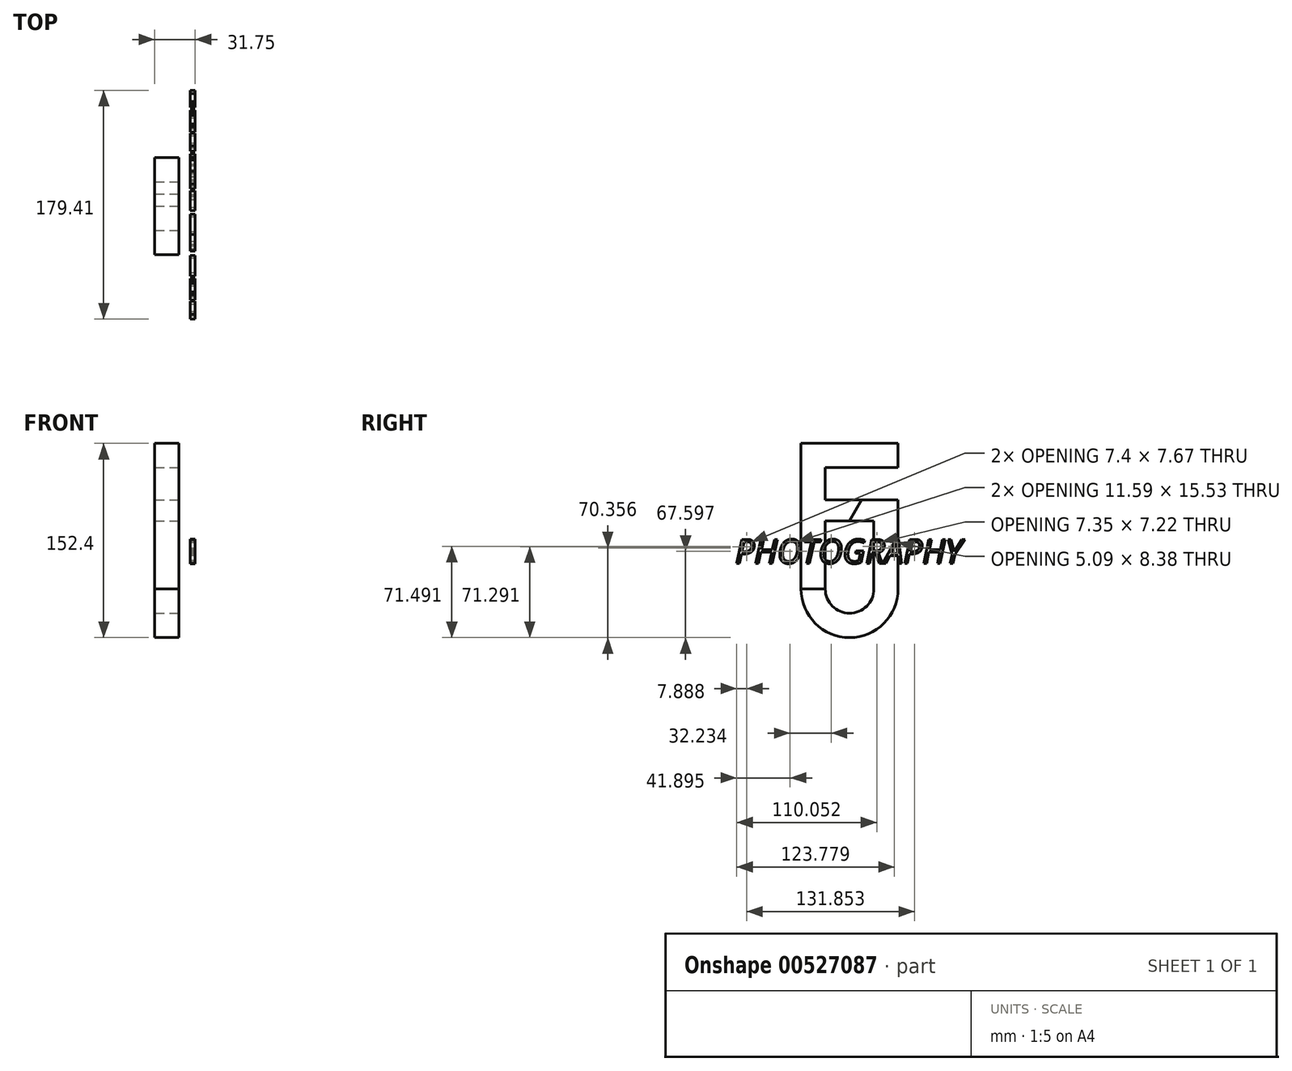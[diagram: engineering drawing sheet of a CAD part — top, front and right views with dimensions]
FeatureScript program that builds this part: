
annotation { "Feature Type Name" : "Feature", "Feature Type Description" : "" }
export const myFeature = defineFeature(function(context is Context, id is Id, definition is map)
    precondition{}
    {
        {
            var Q0;
            Q0=qCreatedBy(makeId("Right.planeOp"),FACE);
            var sketch = newSketch(context, id + "F0", { "sketchPlane" : qUnion([Q0])});
            skArc(sketch, "E0", {"start": v(-38.1, 0) * mm, "mid": v(0, -38.1) * mm, "end": v(38.1, 0) * mm});
            skArc(sketch, "E1", {"start": v(-19.05, 0) * mm, "mid": v(0, -19.05) * mm, "end": v(19.05, 0) * mm});
            skLineSegment(sketch, "E2", {"start": v(-38.1, 0) * mm, "end": v(-19.05, 0) * mm});
            skPoint(sketch, "E3.orphan", {"position": v(-52.53, 0) * mm});
            skLineSegment(sketch, "E4.top", {"start": v(-38.1, 114.3) * mm, "end": v(38.1, 114.3) * mm});
            skLineSegment(sketch, "E5", {"start": v(-19.05, 0) * mm, "end": v(-19.05, 53.35) * mm});
            skLineSegment(sketch, "E6", {"start": v(19.05, 0) * mm, "end": v(19.05, 53.35) * mm});
            skLineSegment(sketch, "E7", {"start": v(-19.05, 69.85) * mm, "end": v(9.52, 69.85) * mm});
            skPoint(sketch, "E8.start.orphan", {"position": v(24.72, 69.46) * mm});
            skPoint(sketch, "E9.trimOffspring.end.orphan", {"position": v(-24.72, 69.46) * mm});
            skLineSegment(sketch, "E10.trimOffspring", {"start": v(38.1, 95.25) * mm, "end": v(-19.05, 95.25) * mm});
            skLineSegment(sketch, "E11.trimOffspring", {"start": v(-19.05, 69.85) * mm, "end": v(-19.05, 95.25) * mm});
            skLineSegment(sketch, "E12", {"start": v(-38.1, 0) * mm, "end": v(-38.1, 114.3) * mm});
            skLineSegment(sketch, "E13", {"start": v(38.1, 0) * mm, "end": v(38.1, 69.85) * mm});
            skLineSegment(sketch, "E14.trimOffspring", {"start": v(38.1, 95.25) * mm, "end": v(38.1, 114.3) * mm});
            skLineSegment(sketch, "E15", {"start": v(-19.05, 53.35) * mm, "end": v(0, 53.35) * mm});
            skLineSegment(sketch, "E16", {"start": v(0, 53.35) * mm, "end": v(9.52, 69.85) * mm});
            skLineSegment(sketch, "E17", {"start": v(0, 53.35) * mm, "end": v(19.05, 53.35) * mm});
            skLineSegment(sketch, "E18", {"start": v(9.52, 69.85) * mm, "end": v(38.1, 69.85) * mm});
            skSolve(sketch);
        }
        {
            var Q0;
            Q0=makeQuery(id+"F0.imprint","IMPRINT",FACE,{"disambiguationData":[TD([[makeQuery(id+"F0.imprint","IMPRINT",EDGE,{"derivedFrom":sQuery(id+"F0.wireOp",EDGE,"E4.top")}),-1.0]])]});
            extrude(context, id + "F1", {"entities" : qUnion([Q0]), "oppositeDirection" : true, "depth" : 19.05 * mm, "offsetDistance" : 25.4 * mm});
        }
        {
            var Q0;
            Q0=makeQuery(id+"F0.imprint","IMPRINT",FACE,{"disambiguationData":[TD([[makeQuery(id+"F0.imprint","IMPRINT",EDGE,{"derivedFrom":sQuery(id+"F0.wireOp",EDGE,"E0")}),1.0]])]});
            extrude(context, id + "F2", {"entities" : qUnion([Q0]), "oppositeDirection" : true, "depth" : 19.05 * mm, "offsetDistance" : 25.4 * mm});
        }
        {
            var Q0;
            Q0=makeQuery(id+"F1.opExtrude","CAP_FACE",FACE,{"disambiguationData":[OSD([sQuery(id+"F0.wireOp",EDGE,"E2"),sQuery(id+"F0.wireOp",EDGE,"E4.top"),sQuery(id+"F0.wireOp",EDGE,"E5"),sQuery(id+"F0.wireOp",EDGE,"E7"),sQuery(id+"F0.wireOp",EDGE,"E10.trimOffspring"),sQuery(id+"F0.wireOp",EDGE,"E11.trimOffspring"),sQuery(id+"F0.wireOp",EDGE,"E12"),sQuery(id+"F0.wireOp",EDGE,"E14.trimOffspring"),sQuery(id+"F0.wireOp",EDGE,"E15"),sQuery(id+"F0.wireOp",EDGE,"E16")])],"isStart":true});
            var sketch = newSketch(context, id + "F3", { "sketchPlane" : qUnion([Q0])});
            skText(sketch, "E19", { "text": "PHOTOGRAPHY", "fontName": "OpenSans-Italic.ttf"});
            const initialGuessF3  = {"E19": [-0.08971, 0.02004, 1, 0, 0.01905]};
            skSetInitialGuess(sketch, initialGuessF3);
            skSolve(sketch);
        }
        {
            var Q0;
            Q0 = qSketchRegion(id + "F3", true);
            extrude(context, id + "F4", {"entities" : qUnion([Q0]), "oppositeDirection" : true, "depth" : -12.7 * mm, "offsetDistance" : 25.4 * mm, "hasSecondDirection" : true, "secondDirectionOppositeDirection" : false, "secondDirectionDepth" : 8.9 * mm});
        }
    });
